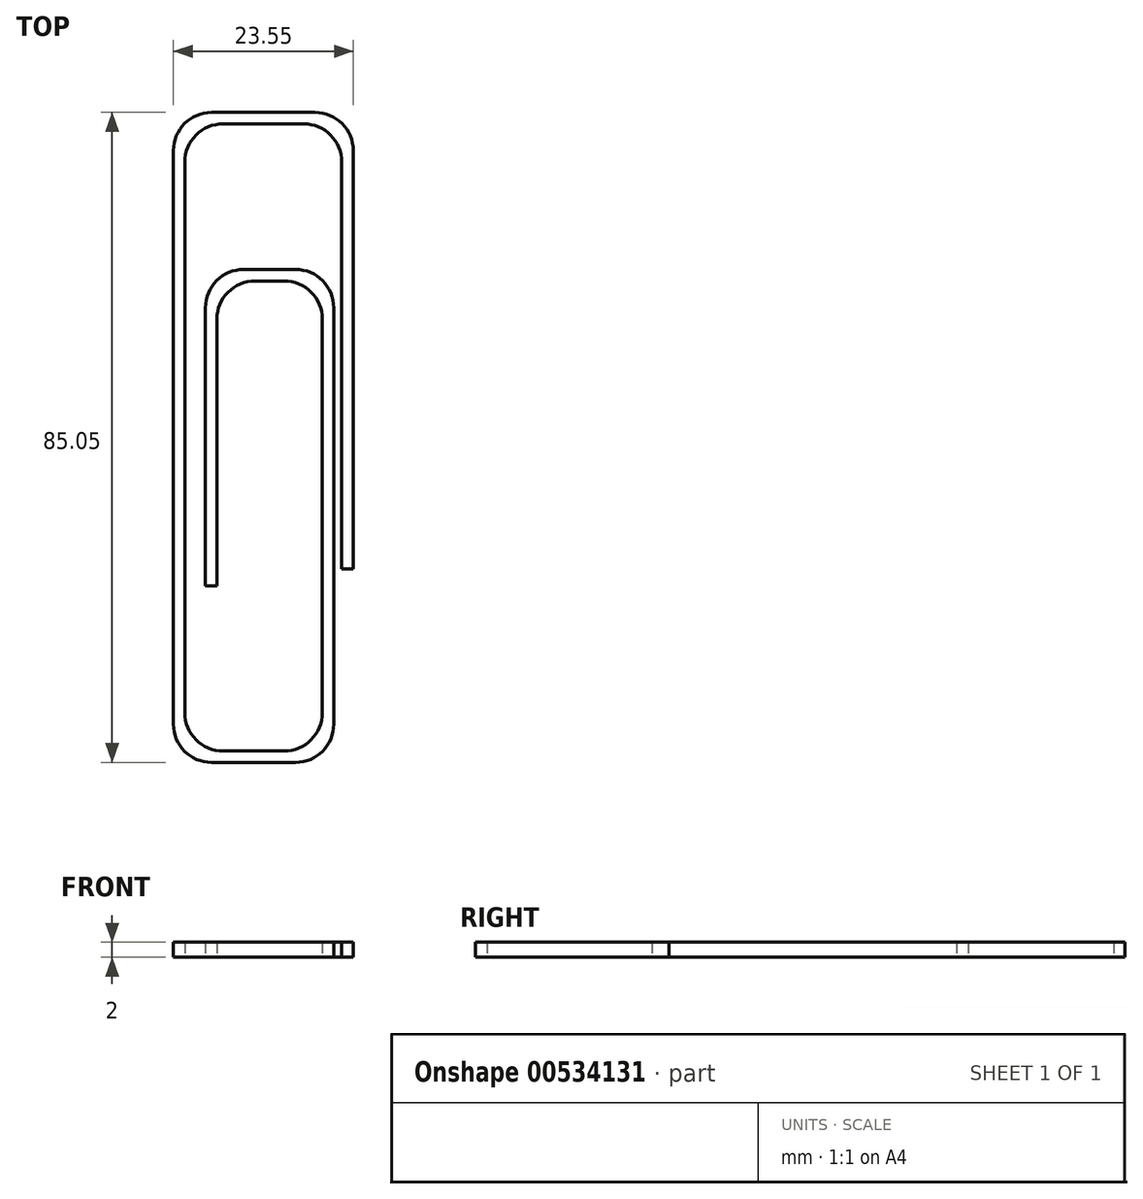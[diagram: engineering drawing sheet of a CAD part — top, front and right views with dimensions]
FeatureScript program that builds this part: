
annotation { "Feature Type Name" : "Feature", "Feature Type Description" : "" }
export const myFeature = defineFeature(function(context is Context, id is Id, definition is map)
    precondition{}
    {
        {
            var Q0;
            Q0=qCreatedBy(makeId("Top.planeOp"),FACE);
            var sketch = newSketch(context, id + "F0", { "sketchPlane" : qUnion([Q0])});
            skLineSegment(sketch, "E0", {"start": v(12.3, -17.2) * mm, "end": v(13.8, -17.2) * mm});
            skLineSegment(sketch, "E1", {"start": v(13.8, -17.2) * mm, "end": v(13.8, 42.5) * mm});
            skLineSegment(sketch, "E2", {"start": v(13.8, 42.5) * mm, "end": v(-9.76, 42.5) * mm});
            skLineSegment(sketch, "E3", {"start": v(-9.76, 42.5) * mm, "end": v(-9.76, -42.56) * mm});
            skLineSegment(sketch, "E4", {"start": v(-9.76, -42.56) * mm, "end": v(11.24, -42.56) * mm});
            skLineSegment(sketch, "E5", {"start": v(11.24, -42.56) * mm, "end": v(11.24, 21.94) * mm});
            skLineSegment(sketch, "E6", {"start": v(11.24, 21.94) * mm, "end": v(-5.56, 21.94) * mm});
            skLineSegment(sketch, "E7", {"start": v(-5.56, 21.94) * mm, "end": v(-5.56, -19.46) * mm});
            skLineSegment(sketch, "E8", {"start": v(-5.56, -19.46) * mm, "end": v(-4.06, -19.46) * mm});
            skLineSegment(sketch, "E9", {"start": v(-4.06, -19.46) * mm, "end": v(-4.06, 20.44) * mm});
            skLineSegment(sketch, "E10", {"start": v(-4.06, 20.44) * mm, "end": v(9.74, 20.44) * mm});
            skLineSegment(sketch, "E11", {"start": v(9.74, 20.44) * mm, "end": v(9.74, -41.06) * mm});
            skLineSegment(sketch, "E12", {"start": v(9.74, -41.06) * mm, "end": v(-8.26, -41.06) * mm});
            skLineSegment(sketch, "E13", {"start": v(-8.26, -41.06) * mm, "end": v(-8.26, 41) * mm});
            skLineSegment(sketch, "E14", {"start": v(-8.26, 41) * mm, "end": v(12.3, 41) * mm});
            skLineSegment(sketch, "E15", {"start": v(12.3, 41) * mm, "end": v(12.3, -17.2) * mm});
            skSolve(sketch);
        }
        {
            var Q0;
            Q0=makeQuery(id+"F0.imprint","IMPRINT",FACE,{"disambiguationData":[TD([[makeQuery(id+"F0.imprint","IMPRINT",EDGE,{"derivedFrom":sQuery(id+"F0.wireOp",EDGE,"E0")}),1.0]])]});
            extrude(context, id + "F1", {"entities" : qUnion([Q0]), "depth" : 2 * mm, "offsetDistance" : 25 * mm});
        }
        {
            var Q0;
            Q0=makeQuery(id+"F1.opExtrude","SWEPT_EDGE",EDGE,{"disambiguationData":[OSD([sQuery(id+"F0.wireOp",EDGE,"E2"),sQuery(id+"F0.wireOp",EDGE,"E3")])]});
            var Q1;
            Q1=makeQuery(id+"F1.opExtrude","SWEPT_EDGE",EDGE,{"disambiguationData":[OSD([sQuery(id+"F0.wireOp",EDGE,"E13"),sQuery(id+"F0.wireOp",EDGE,"E14")])]});
            var Q2;
            Q2=makeQuery(id+"F1.opExtrude","SWEPT_EDGE",EDGE,{"disambiguationData":[OSD([sQuery(id+"F0.wireOp",EDGE,"E14"),sQuery(id+"F0.wireOp",EDGE,"E15")])]});
            var Q3;
            Q3=makeQuery(id+"F1.opExtrude","SWEPT_EDGE",EDGE,{"disambiguationData":[OSD([sQuery(id+"F0.wireOp",EDGE,"E1"),sQuery(id+"F0.wireOp",EDGE,"E2")])]});
            var Q4;
            Q4=makeQuery(id+"F1.opExtrude","SWEPT_EDGE",EDGE,{"disambiguationData":[OSD([sQuery(id+"F0.wireOp",EDGE,"E3"),sQuery(id+"F0.wireOp",EDGE,"E4")])]});
            var Q5;
            Q5=makeQuery(id+"F1.opExtrude","SWEPT_EDGE",EDGE,{"disambiguationData":[OSD([sQuery(id+"F0.wireOp",EDGE,"E12"),sQuery(id+"F0.wireOp",EDGE,"E13")])]});
            var Q6;
            Q6=makeQuery(id+"F1.opExtrude","SWEPT_EDGE",EDGE,{"disambiguationData":[OSD([sQuery(id+"F0.wireOp",EDGE,"E11"),sQuery(id+"F0.wireOp",EDGE,"E12")])]});
            var Q7;
            Q7=makeQuery(id+"F1.opExtrude","SWEPT_EDGE",EDGE,{"disambiguationData":[OSD([sQuery(id+"F0.wireOp",EDGE,"E4"),sQuery(id+"F0.wireOp",EDGE,"E5")])]});
            var Q8;
            Q8=makeQuery(id+"F1.opExtrude","SWEPT_EDGE",EDGE,{"disambiguationData":[OSD([sQuery(id+"F0.wireOp",EDGE,"E6"),sQuery(id+"F0.wireOp",EDGE,"E7")])]});
            var Q9;
            Q9=makeQuery(id+"F1.opExtrude","SWEPT_EDGE",EDGE,{"disambiguationData":[OSD([sQuery(id+"F0.wireOp",EDGE,"E5"),sQuery(id+"F0.wireOp",EDGE,"E6")])]});
            var Q10;
            Q10=makeQuery(id+"F1.opExtrude","SWEPT_EDGE",EDGE,{"disambiguationData":[OSD([sQuery(id+"F0.wireOp",EDGE,"E10"),sQuery(id+"F0.wireOp",EDGE,"E11")])]});
            var Q11;
            Q11=makeQuery(id+"F1.opExtrude","SWEPT_EDGE",EDGE,{"disambiguationData":[OSD([sQuery(id+"F0.wireOp",EDGE,"E9"),sQuery(id+"F0.wireOp",EDGE,"E10")])]});
            fillet(context, id + "F2", {"entities" : qUnion([Q0, Q1, Q2, Q3, Q4, Q5, Q6, Q7, Q8, Q9, Q10, Q11]), "radius" : 5 * mm, "tangentPropagation" : true, "allowEdgeOverflow" : false});
        }
    });
